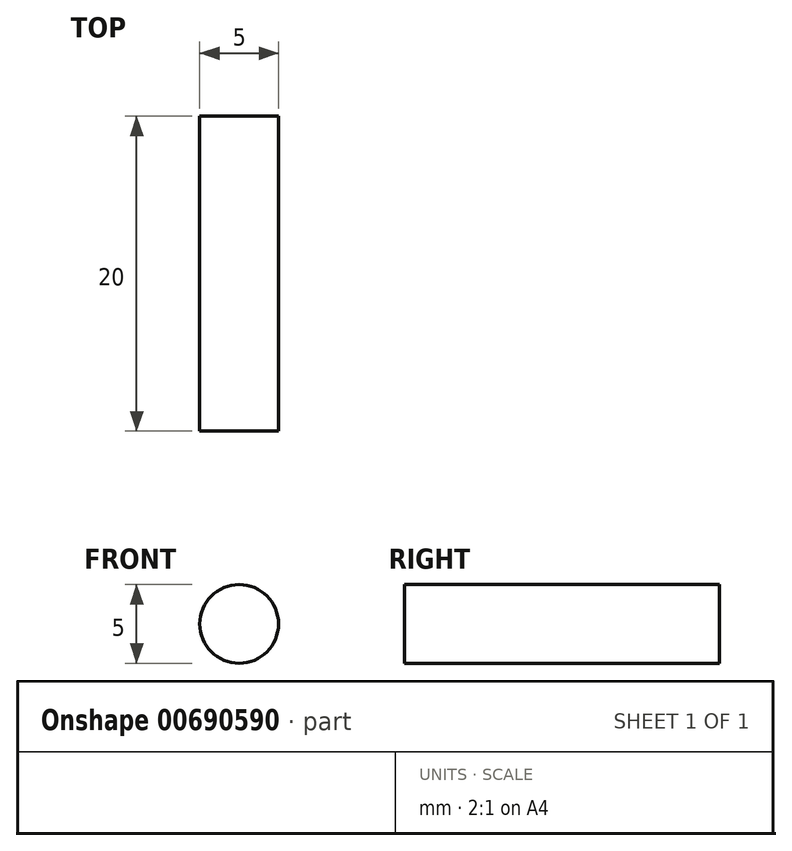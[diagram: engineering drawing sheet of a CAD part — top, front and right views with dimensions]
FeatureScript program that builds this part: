
annotation { "Feature Type Name" : "Feature", "Feature Type Description" : "" }
export const myFeature = defineFeature(function(context is Context, id is Id, definition is map)
    precondition{}
    {
        {
            var Q0;
            Q0=qCreatedBy(makeId("Front.planeOp"),FACE);
            var sketch = newSketch(context, id + "F0", { "sketchPlane" : qUnion([Q0])});
            skCircle(sketch, "E0", {"center": v(0, 0) * mm, "radius": 2.5 * mm});
            skSolve(sketch);
        }
        {
            var Q0;
            Q0=makeQuery(id+"F0.imprint","IMPRINT",FACE,{"disambiguationData":[TD([[makeQuery(id+"F0.imprint","IMPRINT",EDGE,{"derivedFrom":sQuery(id+"F0.wireOp",EDGE,"E0")}),1.0]])]});
            extrude(context, id + "F1", {"entities" : qUnion([Q0]), "depth" : 20 * mm, "offsetDistance" : 25 * mm});
        }
    });
